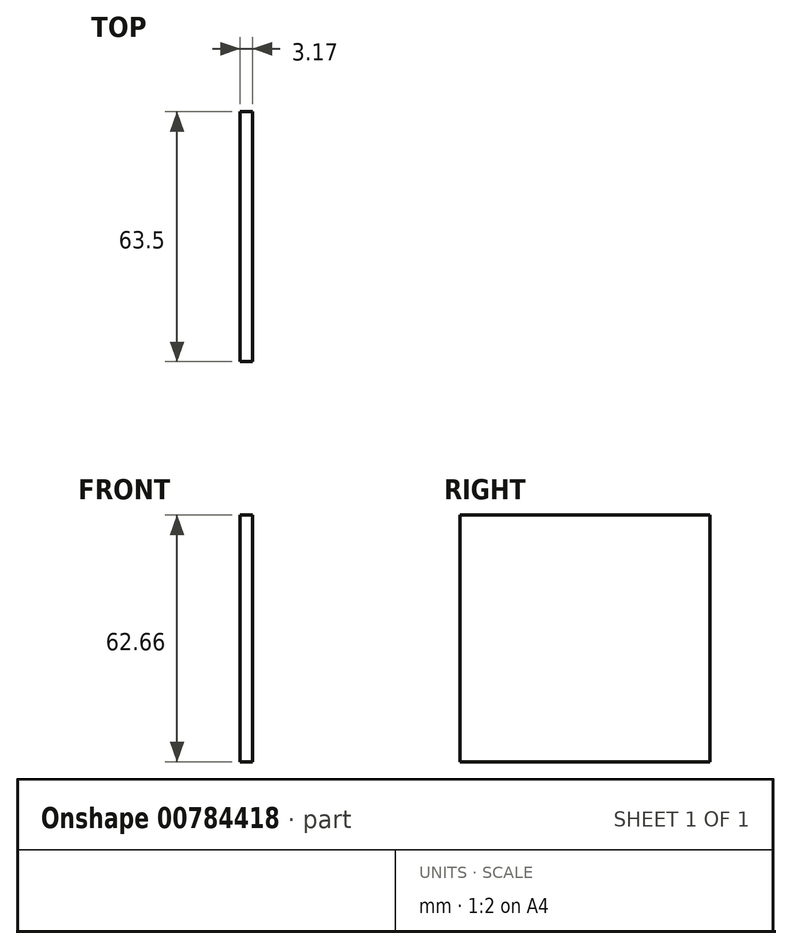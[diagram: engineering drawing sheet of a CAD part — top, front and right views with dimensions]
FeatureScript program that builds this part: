
annotation { "Feature Type Name" : "Feature", "Feature Type Description" : "" }
export const myFeature = defineFeature(function(context is Context, id is Id, definition is map)
    precondition{}
    {
        {
            var Q0;
            Q0=qCreatedBy(makeId("Right.planeOp"),FACE);
            var sketch = newSketch(context, id + "F0", { "sketchPlane" : qUnion([Q0])});
            skLineSegment(sketch, "E0.bottom", {"start": v(29.14, 33.5) * mm, "end": v(-34.36, 33.5) * mm});
            skLineSegment(sketch, "E0.top", {"start": v(29.14, -29.16) * mm, "end": v(-34.36, -29.16) * mm});
            skLineSegment(sketch, "E0.left", {"start": v(29.14, 33.5) * mm, "end": v(29.14, -29.16) * mm});
            skLineSegment(sketch, "E0.right", {"start": v(-34.36, 33.5) * mm, "end": v(-34.36, -29.16) * mm});
            skSolve(sketch);
        }
        {
            var Q0;
            Q0=makeQuery(id+"F0.imprint","IMPRINT",FACE,{"disambiguationData":[TD([[makeQuery(id+"F0.imprint","IMPRINT",EDGE,{"derivedFrom":sQuery(id+"F0.wireOp",EDGE,"E0.bottom")}),1.0]])]});
            extrude(context, id + "F1", {"entities" : qUnion([Q0]), "depth" : 3.17 * mm, "offsetDistance" : 25.4 * mm});
        }
    });
